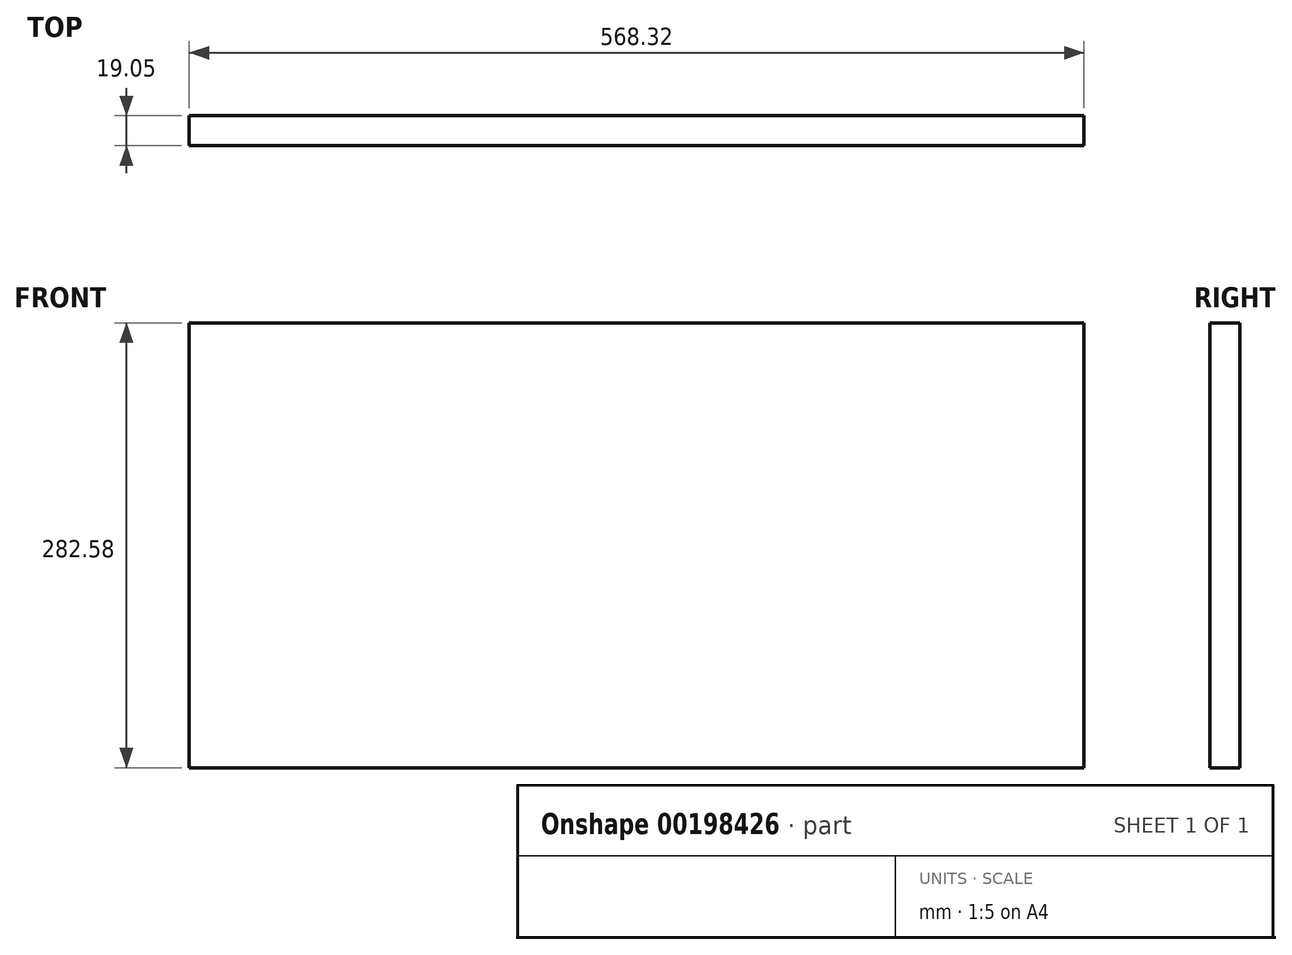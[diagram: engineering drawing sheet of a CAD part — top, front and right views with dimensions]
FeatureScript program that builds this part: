
annotation { "Feature Type Name" : "Feature", "Feature Type Description" : "" }
export const myFeature = defineFeature(function(context is Context, id is Id, definition is map)
    precondition{}
    {
        {
            var Q0;
            Q0=qCreatedBy(makeId("Front.planeOp"),FACE);
            var sketch = newSketch(context, id + "F0", { "sketchPlane" : qUnion([Q0])});
            skLineSegment(sketch, "E0.bottom", {"start": v(-284.16, 141.29) * mm, "end": v(284.16, 141.29) * mm});
            skLineSegment(sketch, "E0.top", {"start": v(-284.16, -141.29) * mm, "end": v(284.16, -141.29) * mm});
            skLineSegment(sketch, "E0.left", {"start": v(-284.16, 141.29) * mm, "end": v(-284.16, -141.29) * mm});
            skLineSegment(sketch, "E0.right", {"start": v(284.16, 141.29) * mm, "end": v(284.16, -141.29) * mm});
            skPoint(sketch, "E0.middle", {"position": v(0, 0) * mm});
            skSolve(sketch);
        }
        {
            var Q0;
            Q0=makeQuery(id+"F0.imprint","IMPRINT",FACE,{"disambiguationData":[TD([[makeQuery(id+"F0.imprint","IMPRINT",EDGE,{"derivedFrom":sQuery(id+"F0.wireOp",EDGE,"E0.bottom")}),-1.0]])]});
            extrude(context, id + "F1", {"entities" : qUnion([Q0]), "depth" : 19.05 * mm});
        }
    });
